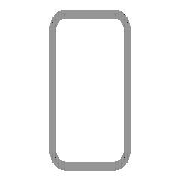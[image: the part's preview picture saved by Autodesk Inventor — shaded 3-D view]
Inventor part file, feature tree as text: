
AUTODESK INVENTOR PART (.ipt)
format: ipt  version: 2025 (Build 290162010, 162A)  size: 133,120 bytes
history: native  units: mm (DEFAULTED — no unit token found)
features: other x4, sketch x1, plane x1
ambient origin geometry x8: Origin, YZ Plane, XZ Plane, XY Plane, X Axis, Y Axis, Z Axis, Center Point
bodies: Solid1 (feature_tree), Body (feature_tree)
feature tree (6):
  parser-record x1  (decoder bookkeeping rows leaked as tree rows — omitted from the tree; the rows remain in map.json)
  other  "Driven Length"
  other  "Start Plane"
  other  "End Plane"
  sketch  "Sketch3"  dims[d3=2000.0mm d4=0.0mm d7=6.0mm d9=40.0mm d11=80.0mm d12=3.0mm d13=-0.0mm d14=2000.0mm d15=20.0mm d16=40.0mm d17=90.0deg d18=2000.0mm]
  plane  "Work Plane3"
